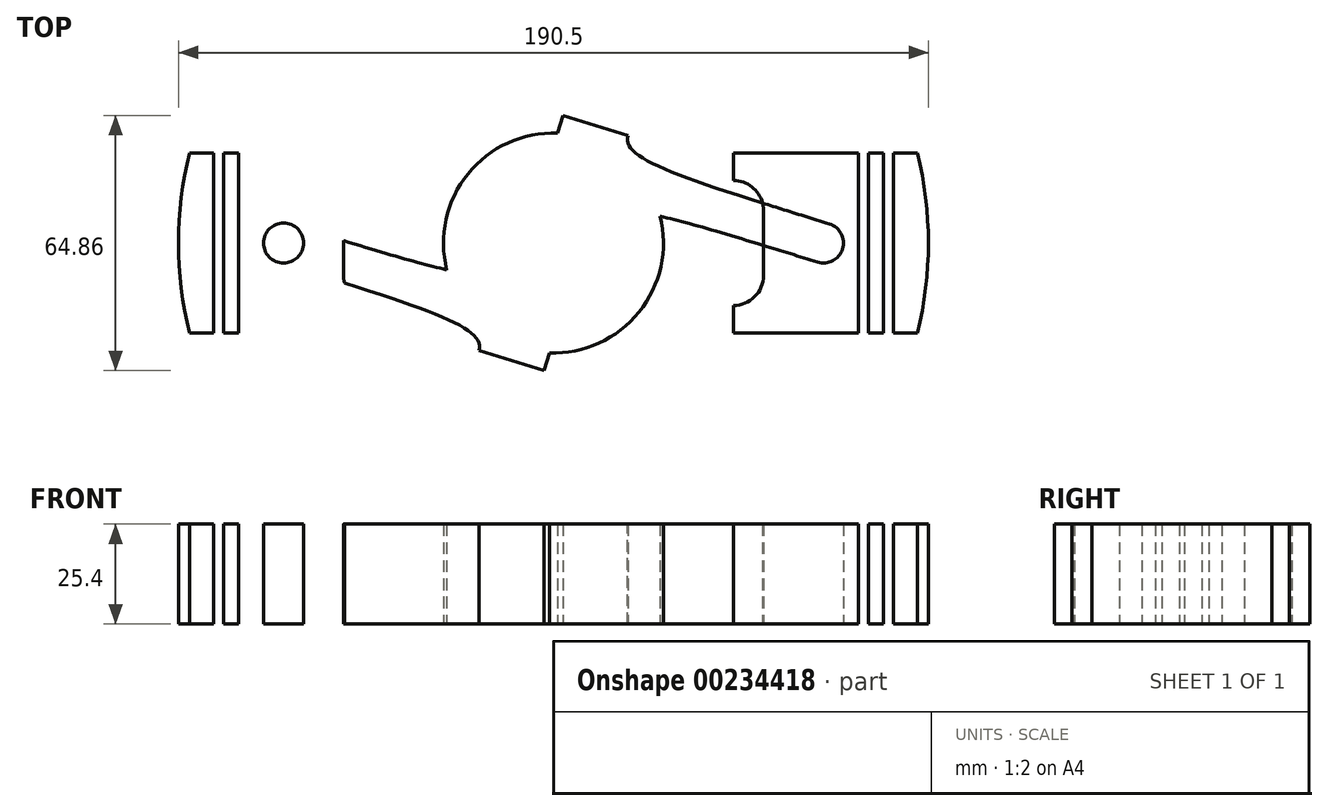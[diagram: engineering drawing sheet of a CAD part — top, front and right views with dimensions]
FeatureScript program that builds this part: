
annotation { "Feature Type Name" : "Feature", "Feature Type Description" : "" }
export const myFeature = defineFeature(function(context is Context, id is Id, definition is map)
    precondition{}
    {
        {
            var Q0;
            Q0=qCreatedBy(makeId("Top.planeOp"),FACE);
            var sketch = newSketch(context, id + "F1", { "sketchPlane" : qUnion([Q0])});
            skLineSegment(sketch, "E0", {"start": v(45.72, 22.86) * mm, "end": v(45.72, 15.88) * mm});
            skLineSegment(sketch, "E1", {"start": v(86.36, 22.86) * mm, "end": v(86.36, -22.86) * mm});
            skLineSegment(sketch, "E2", {"start": v(80.01, 22.86) * mm, "end": v(80.01, -22.86) * mm});
            skLineSegment(sketch, "E3", {"start": v(77.47, 22.86) * mm, "end": v(77.47, -22.86) * mm});
            skLineSegment(sketch, "E4", {"start": v(45.72, 15.88) * mm, "end": v(45.72, 15.88) * mm});
            skLineSegment(sketch, "E5", {"start": v(53.34, 8.26) * mm, "end": v(53.34, -8.25) * mm});
            skLineSegment(sketch, "E6", {"start": v(45.72, -15.88) * mm, "end": v(45.72, -15.88) * mm});
            skPoint(sketch, "E7.visualSharp", {"position": v(53.34, 15.88) * mm});
            skArc(sketch, "E7.filletArc", {"start": v(53.34, 8.26) * mm, "mid": v(51.1, 13.64) * mm, "end": v(45.72, 15.88) * mm});
            skPoint(sketch, "E8.visualSharp", {"position": v(53.34, -15.87) * mm});
            skArc(sketch, "E8.filletArc", {"start": v(45.72, -15.88) * mm, "mid": v(51.1, -13.64) * mm, "end": v(53.34, -8.25) * mm});
            skLineSegment(sketch, "E9", {"start": v(0, 0) * mm, "end": v(45.72, 0) * mm, "construction": true});
            skLineSegment(sketch, "E10", {"start": v(45.72, 0) * mm, "end": v(53.34, 0) * mm, "construction": true});
            skLineSegment(sketch, "E11", {"start": v(77.47, 0) * mm, "end": v(80.01, 0) * mm, "construction": true});
            skLineSegment(sketch, "E12", {"start": v(80.01, 0) * mm, "end": v(83.82, 0) * mm, "construction": true});
            skLineSegment(sketch, "E13", {"start": v(83.82, 0) * mm, "end": v(86.36, 0) * mm, "construction": true});
            skLineSegment(sketch, "E14", {"start": v(53.34, 0) * mm, "end": v(68.58, 0) * mm, "construction": true});
            skLineSegment(sketch, "E15", {"start": v(68.58, 0) * mm, "end": v(77.47, 0) * mm, "construction": true});
            skCircle(sketch, "E16", {"center": v(68.58, 0) * mm, "radius": 5.08 * mm});
            skLineSegment(sketch, "E17", {"start": v(0, 95.25) * mm, "end": v(0, -95.25) * mm, "construction": true});
            skLineSegment(sketch, "E18", {"start": v(2.4, 32.43) * mm, "end": v(1, 27.92) * mm});
            skFitSpline(sketch, "E19", {"points": [v(18.9, 27.3) * mm, v(70.09, 4.85) * mm], "startDerivative": vector(-5.58, -18) * mm, "endDerivative": vector(113.06, -35.07) * mm});
            skLineSegment(sketch, "E20", {"start": v(68.58, 0) * mm, "end": v(8.56, 18.62) * mm, "construction": true});
            skPoint(sketch, "E21.MirrorCS.1.internal.orphan", {"position": v(67.07, -4.85) * mm});
            skLineSegment(sketch, "E22.trimOffspring", {"start": v(80.01, -22.86) * mm, "end": v(83.82, -22.86) * mm});
            skLineSegment(sketch, "E23.trimOffspring", {"start": v(45.72, -22.86) * mm, "end": v(77.47, -22.86) * mm});
            skLineSegment(sketch, "E24.MirrorCS", {"start": v(17.05, 21.3) * mm, "end": v(18.9, 27.3) * mm, "construction": true});
            skLineSegment(sketch, "E25.MirrorCS", {"start": v(80.01, 22.86) * mm, "end": v(83.82, 22.86) * mm});
            skLineSegment(sketch, "E26.MirrorCS", {"start": v(45.72, -15.88) * mm, "end": v(45.72, -22.86) * mm});
            skLineSegment(sketch, "E27.MirrorCS", {"start": v(83.82, 22.86) * mm, "end": v(83.82, -22.86) * mm});
            skLineSegment(sketch, "E28.MirrorCS", {"start": v(18.9, 27.3) * mm, "end": v(2.4, 32.43) * mm});
            skLineSegment(sketch, "E29.MirrorCS", {"start": v(45.72, 22.86) * mm, "end": v(77.47, 22.86) * mm});
            skFitSpline(sketch, "E30.MirrorCS", {"points": [v(12.18, 5.6) * mm, v(67.07, -4.85) * mm], "startDerivative": vector(5.58, 18) * mm, "endDerivative": vector(113.06, -35.07) * mm});
            skArc(sketch, "E31", {"start": v(92.47, 22.86) * mm, "mid": v(95.25, 0) * mm, "end": v(92.47, -22.86) * mm});
            skLineSegment(sketch, "E32", {"start": v(86.36, 22.86) * mm, "end": v(92.47, 22.86) * mm});
            skLineSegment(sketch, "E33", {"start": v(86.36, -22.86) * mm, "end": v(92.47, -22.86) * mm});
            skCircle(sketch, "E34.MirrorC", {"center": v(-68.58, 0) * mm, "radius": 5.08 * mm});
            skLineSegment(sketch, "E35.MirrorCS", {"start": v(-53.34, 8.26) * mm, "end": v(-53.34, -8.25) * mm});
            skArc(sketch, "E36.MirrorCS", {"start": v(-45.72, -15.88) * mm, "mid": v(-51.1, -13.64) * mm, "end": v(-53.34, -8.25) * mm});
            skArc(sketch, "E37.MirrorCS", {"start": v(-53.34, 8.26) * mm, "mid": v(-51.1, 13.64) * mm, "end": v(-45.72, 15.88) * mm});
            skLineSegment(sketch, "E38.MirrorCS", {"start": v(-45.72, 22.86) * mm, "end": v(-45.72, 15.88) * mm});
            skLineSegment(sketch, "E39.MirrorCS", {"start": v(-45.72, -15.88) * mm, "end": v(-45.72, -22.86) * mm});
            skLineSegment(sketch, "E40.MirrorCS", {"start": v(-45.72, -22.86) * mm, "end": v(-77.47, -22.86) * mm});
            skLineSegment(sketch, "E41.MirrorCS", {"start": v(-80.01, -22.86) * mm, "end": v(-83.82, -22.86) * mm});
            skLineSegment(sketch, "E42.MirrorCS", {"start": v(-86.36, -22.86) * mm, "end": v(-92.47, -22.86) * mm});
            skLineSegment(sketch, "E43.MirrorCS", {"start": v(-83.82, 22.86) * mm, "end": v(-83.82, -22.86) * mm});
            skLineSegment(sketch, "E44.MirrorCS", {"start": v(-80.01, 22.86) * mm, "end": v(-80.01, -22.86) * mm});
            skLineSegment(sketch, "E45.MirrorCS", {"start": v(-77.47, 22.86) * mm, "end": v(-77.47, -22.86) * mm});
            skLineSegment(sketch, "E46.MirrorCS", {"start": v(-45.72, 22.86) * mm, "end": v(-77.47, 22.86) * mm});
            skLineSegment(sketch, "E47.MirrorCS", {"start": v(-80.01, 22.86) * mm, "end": v(-83.82, 22.86) * mm});
            skLineSegment(sketch, "E48.MirrorCS", {"start": v(-86.36, 22.86) * mm, "end": v(-92.47, 22.86) * mm});
            skLineSegment(sketch, "E49.MirrorCS", {"start": v(-86.36, 22.86) * mm, "end": v(-86.36, -22.86) * mm});
            skArc(sketch, "E50.MirrorCS", {"start": v(-92.47, 22.86) * mm, "mid": v(-95.25, 0) * mm, "end": v(-92.47, -22.86) * mm});
            skLineSegment(sketch, "E51.MirrorCS", {"start": v(-18.9, -27.3) * mm, "end": v(-2.4, -32.43) * mm});
            skLineSegment(sketch, "E52.MirrorCS", {"start": v(-2.4, -32.43) * mm, "end": v(-1, -27.92) * mm});
            skFitSpline(sketch, "E53.MirrorCS", {"points": [v(-18.9, -27.3) * mm, v(-70.09, -4.85) * mm], "startDerivative": vector(5.58, 18) * mm, "endDerivative": vector(-113.06, 35.07) * mm});
            skFitSpline(sketch, "E54.MirrorCS", {"points": [v(-12.18, -5.6) * mm, v(-67.07, 4.85) * mm], "startDerivative": vector(-5.58, -18) * mm, "endDerivative": vector(-113.06, 35.07) * mm});
            skCircle(sketch, "E55", {"center": v(0, 0) * mm, "radius": 27.94 * mm});
            skSolve(sketch);
        }
        {
            var Q0;
            {var subQ0=sQuery(id+"F1.wireOp",EDGE,"E55");var subQ1=makeQuery(id+"F1.imprint","INTERSECT",VERTEX,{"derivedFrom":[sQuery(id+"F1.wireOp",EDGE,"E18"),subQ0]});Q0=makeQuery(id+"F1.imprint","IMPRINT",FACE,{"disambiguationData":[TD([[makeQuery(id+"F1.imprint","IMPRINT",EDGE,{"disambiguationData":[TD([[subQ1,1.0]])],"derivedFrom":subQ0}),1.0]])]});}
            var Q1;
            Q1=makeQuery(id+"F1.imprint","IMPRINT",FACE,{"disambiguationData":[TD([[makeQuery(id+"F1.imprint","IMPRINT",EDGE,{"derivedFrom":sQuery(id+"F1.wireOp",EDGE,"E51.MirrorCS")}),1.0]])]});
            var Q2;
            Q2=makeQuery(id+"F1.imprint","IMPRINT",FACE,{"disambiguationData":[TD([[makeQuery(id+"F1.imprint","IMPRINT",EDGE,{"derivedFrom":sQuery(id+"F1.wireOp",EDGE,"E34.MirrorC")}),1.0]])]});
            var Q3;
            Q3=makeQuery(id+"F1.imprint","IMPRINT",FACE,{"disambiguationData":[TD([[makeQuery(id+"F1.imprint","IMPRINT",EDGE,{"derivedFrom":sQuery(id+"F1.wireOp",EDGE,"E41.MirrorCS")}),-1.0]])]});
            var Q4;
            Q4=makeQuery(id+"F1.imprint","IMPRINT",FACE,{"disambiguationData":[TD([[makeQuery(id+"F1.imprint","IMPRINT",EDGE,{"derivedFrom":sQuery(id+"F1.wireOp",EDGE,"E42.MirrorCS")}),-1.0]])]});
            var Q5;
            {var subQ4=sQuery(id+"F1.wireOp",EDGE,"E18");Q5=makeQuery(id+"F1.imprint","IMPRINT",FACE,{"disambiguationData":[TD([[makeQuery(id+"F1.imprint","IMPRINT",EDGE,{"derivedFrom":subQ4}),1.0]])]});}
            var Q6;
            {var subQ1=sQuery(id+"F1.wireOp",EDGE,"E0");Q6=makeQuery(id+"F1.imprint","IMPRINT",FACE,{"disambiguationData":[TD([[makeQuery(id+"F1.imprint","IMPRINT",EDGE,{"derivedFrom":subQ1}),1.0]])]});}
            var Q7;
            Q7=makeQuery(id+"F1.imprint","IMPRINT",FACE,{"disambiguationData":[TD([[makeQuery(id+"F1.imprint","IMPRINT",EDGE,{"derivedFrom":sQuery(id+"F1.wireOp",EDGE,"E2")}),1.0]])]});
            var Q8;
            Q8=makeQuery(id+"F1.imprint","IMPRINT",FACE,{"disambiguationData":[TD([[makeQuery(id+"F1.imprint","IMPRINT",EDGE,{"derivedFrom":sQuery(id+"F1.wireOp",EDGE,"E1")}),1.0]])]});
            extrude(context, id + "F0", {"entities" : qUnion([Q0, Q1, Q2, Q3, Q4, Q5, Q6, Q7, Q8]), "depth" : 25.4 * mm});
        }
    });
